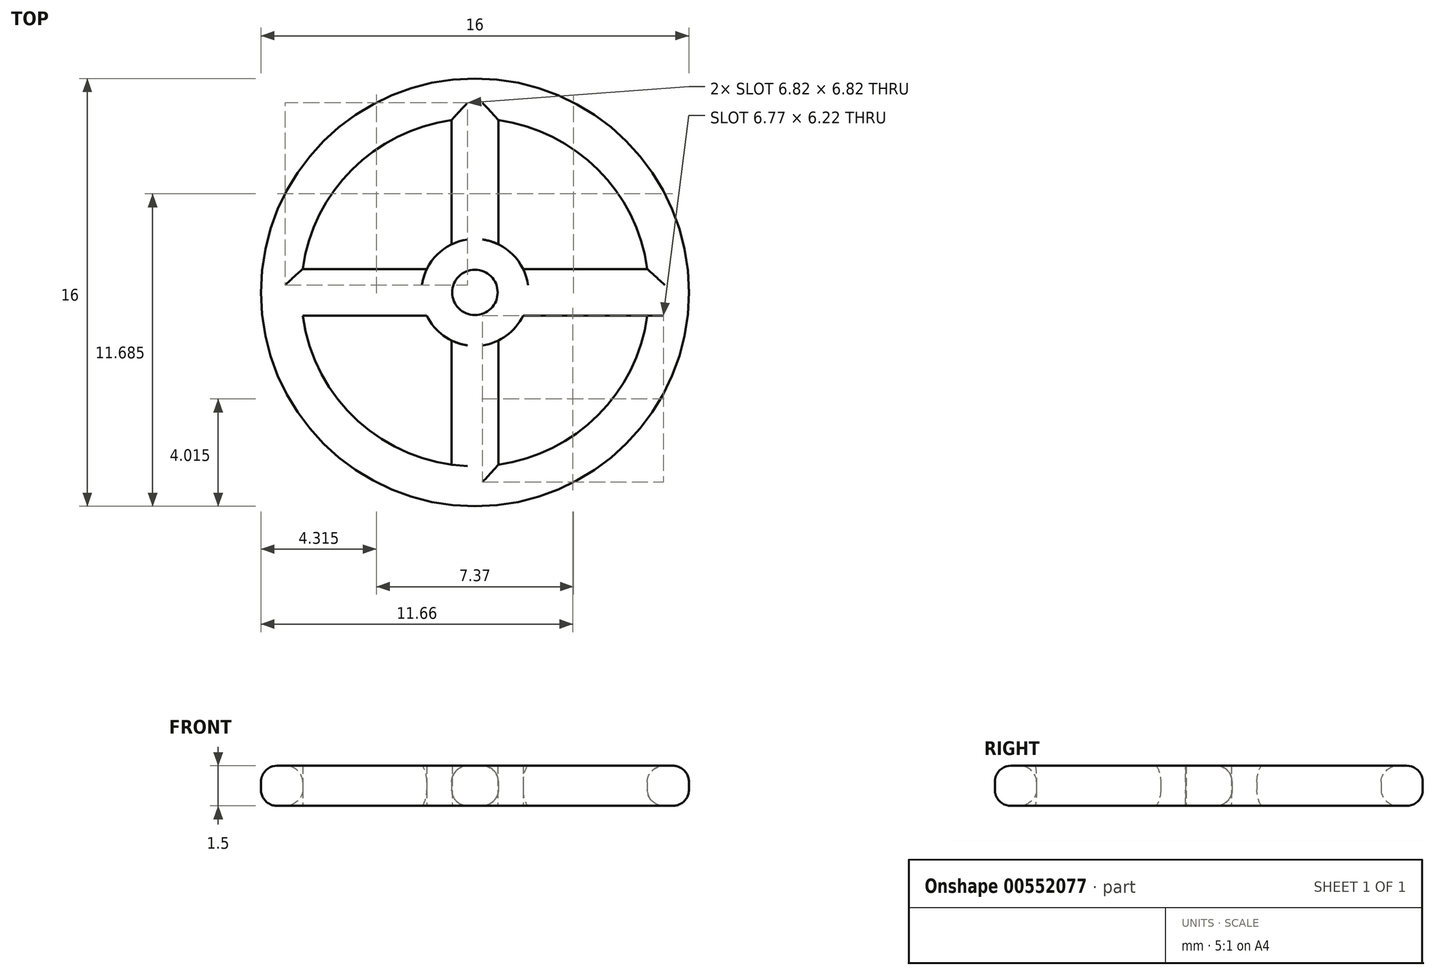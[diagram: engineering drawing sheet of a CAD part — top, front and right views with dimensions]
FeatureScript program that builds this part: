
annotation { "Feature Type Name" : "Feature", "Feature Type Description" : "" }
export const myFeature = defineFeature(function(context is Context, id is Id, definition is map)
    precondition{}
    {
        {
            var Q0;
            Q0=qCreatedBy(makeId("Top.planeOp"),FACE);
            var sketch = newSketch(context, id + "F0", { "sketchPlane" : qUnion([Q0])});
            skCircle(sketch, "E0", {"center": v(0, 0) * mm, "radius": 8 * mm});
            skCircle(sketch, "E1", {"center": v(0, 0) * mm, "radius": 6.5 * mm});
            skLineSegment(sketch, "E2.bottom", {"start": v(7.37, -0.87) * mm, "end": v(-7.37, -0.88) * mm});
            skLineSegment(sketch, "E2.top", {"start": v(7.37, 0.88) * mm, "end": v(-7.37, 0.87) * mm});
            skLineSegment(sketch, "E2.left", {"start": v(7.37, -0.87) * mm, "end": v(7.37, 0.88) * mm});
            skLineSegment(sketch, "E2.right", {"start": v(-7.37, -0.88) * mm, "end": v(-7.37, 0.87) * mm});
            skLineSegment(sketch, "E3.bottom", {"start": v(0.88, 6.98) * mm, "end": v(-0.88, 6.98) * mm});
            skLineSegment(sketch, "E3.top", {"start": v(0.88, -6.98) * mm, "end": v(-0.88, -6.98) * mm});
            skLineSegment(sketch, "E3.left", {"start": v(0.88, 6.98) * mm, "end": v(0.88, -6.98) * mm});
            skLineSegment(sketch, "E3.right", {"start": v(-0.88, 6.98) * mm, "end": v(-0.88, -6.98) * mm});
            skCircle(sketch, "E4", {"center": v(0, 0) * mm, "radius": 0.85 * mm});
            skCircle(sketch, "E5", {"center": v(0, 0) * mm, "radius": 2 * mm});
            skSolve(sketch);
        }
        {
            var Q0;
            {var subQ5=sQuery(id+"F0.wireOp",EDGE,"E2.right");Q0=makeQuery(id+"F0.imprint","IMPRINT",FACE,{"disambiguationData":[TD([[makeQuery(id+"F0.imprint","IMPRINT",EDGE,{"derivedFrom":subQ5}),-1.0]])]});}
            var Q1;
            {var subQ0=sQuery(id+"F0.wireOp",EDGE,"E2.top");var subQ1=sQuery(id+"F0.wireOp",EDGE,"E1");var subQ2=makeQuery(id+"F0.imprint","INTERSECT",VERTEX,{"disambiguationData":[OD(1.0)],"derivedFrom":[subQ1,subQ0]});Q1=makeQuery(id+"F0.imprint","IMPRINT",FACE,{"disambiguationData":[TD([[makeQuery(id+"F0.imprint","IMPRINT",EDGE,{"disambiguationData":[TD([[subQ2,-1.0]])],"derivedFrom":subQ1}),1.0]])]});}
            var Q2;
            Q2=makeQuery(id+"F0.imprint","IMPRINT",FACE,{"disambiguationData":[TD([[makeQuery(id+"F0.imprint","IMPRINT",EDGE,{"derivedFrom":sQuery(id+"F0.wireOp",EDGE,"E0")}),1.0]])]});
            var Q3;
            {var subQ5=sQuery(id+"F0.wireOp",EDGE,"E3.bottom");Q3=makeQuery(id+"F0.imprint","IMPRINT",FACE,{"disambiguationData":[TD([[makeQuery(id+"F0.imprint","IMPRINT",EDGE,{"derivedFrom":subQ5}),1.0]])]});}
            var Q4;
            {var subQ0=sQuery(id+"F0.wireOp",EDGE,"E3.left");var subQ1=sQuery(id+"F0.wireOp",EDGE,"E1");var subQ2=makeQuery(id+"F0.imprint","INTERSECT",VERTEX,{"disambiguationData":[OD(0.0)],"derivedFrom":[subQ1,subQ0]});Q4=makeQuery(id+"F0.imprint","IMPRINT",FACE,{"disambiguationData":[TD([[makeQuery(id+"F0.imprint","IMPRINT",EDGE,{"disambiguationData":[TD([[subQ2,-1.0]])],"derivedFrom":subQ1}),1.0]])]});}
            var Q5;
            {var subQ0=sQuery(id+"F0.wireOp",EDGE,"E5");var subQ1=sQuery(id+"F0.wireOp",EDGE,"E2.top");var subQ2=makeQuery(id+"F0.imprint","INTERSECT",VERTEX,{"disambiguationData":[OD(0.0)],"derivedFrom":[subQ1,subQ0]});Q5=makeQuery(id+"F0.imprint","IMPRINT",FACE,{"disambiguationData":[TD([[makeQuery(id+"F0.imprint","IMPRINT",EDGE,{"disambiguationData":[TD([[subQ2,-1.0]])],"derivedFrom":subQ1}),-1.0]])]});}
            var Q6;
            {var subQ0=sQuery(id+"F0.wireOp",EDGE,"E3.left");var subQ1=sQuery(id+"F0.wireOp",EDGE,"E2.top");var subQ2=makeQuery(id+"F0.imprint","INTERSECT",VERTEX,{"derivedFrom":[subQ1,subQ0]});Q6=makeQuery(id+"F0.imprint","IMPRINT",FACE,{"disambiguationData":[TD([[makeQuery(id+"F0.imprint","IMPRINT",EDGE,{"disambiguationData":[TD([[subQ2,-1.0]])],"derivedFrom":subQ1}),-1.0]])]});}
            var Q7;
            {var subQ0=sQuery(id+"F0.wireOp",EDGE,"E3.right");var subQ1=sQuery(id+"F0.wireOp",EDGE,"E2.top");var subQ2=makeQuery(id+"F0.imprint","INTERSECT",VERTEX,{"derivedFrom":[subQ1,subQ0]});Q7=makeQuery(id+"F0.imprint","IMPRINT",FACE,{"disambiguationData":[TD([[makeQuery(id+"F0.imprint","IMPRINT",EDGE,{"disambiguationData":[TD([[subQ2,-1.0]])],"derivedFrom":subQ1}),-1.0]])]});}
            var Q8;
            {var subQ0=sQuery(id+"F0.wireOp",EDGE,"E3.right");var subQ1=sQuery(id+"F0.wireOp",EDGE,"E2.bottom");var subQ2=makeQuery(id+"F0.imprint","INTERSECT",VERTEX,{"derivedFrom":[subQ1,subQ0]});Q8=makeQuery(id+"F0.imprint","IMPRINT",FACE,{"disambiguationData":[TD([[makeQuery(id+"F0.imprint","IMPRINT",EDGE,{"disambiguationData":[TD([[subQ2,-1.0]])],"derivedFrom":subQ1}),-1.0]])]});}
            var Q9;
            {var subQ0=sQuery(id+"F0.wireOp",EDGE,"E3.right");var subQ1=sQuery(id+"F0.wireOp",EDGE,"E2.bottom");var subQ2=makeQuery(id+"F0.imprint","INTERSECT",VERTEX,{"derivedFrom":[subQ1,subQ0]});Q9=makeQuery(id+"F0.imprint","IMPRINT",FACE,{"disambiguationData":[TD([[makeQuery(id+"F0.imprint","IMPRINT",EDGE,{"disambiguationData":[TD([[subQ2,-1.0]])],"derivedFrom":subQ1}),1.0]])]});}
            var Q10;
            {var subQ0=sQuery(id+"F0.wireOp",EDGE,"E3.left");var subQ1=sQuery(id+"F0.wireOp",EDGE,"E2.bottom");var subQ2=makeQuery(id+"F0.imprint","INTERSECT",VERTEX,{"derivedFrom":[subQ1,subQ0]});Q10=makeQuery(id+"F0.imprint","IMPRINT",FACE,{"disambiguationData":[TD([[makeQuery(id+"F0.imprint","IMPRINT",EDGE,{"disambiguationData":[TD([[subQ2,-1.0]])],"derivedFrom":subQ1}),1.0]])]});}
            var Q11;
            Q11=makeQuery(id+"F0.imprint","IMPRINT",FACE,{"disambiguationData":[TD([[makeQuery(id+"F0.imprint","IMPRINT",EDGE,{"derivedFrom":sQuery(id+"F0.wireOp",EDGE,"E4")}),-1.0]])]});
            var Q12;
            {var subQ0=sQuery(id+"F0.wireOp",EDGE,"E5");var subQ1=sQuery(id+"F0.wireOp",EDGE,"E2.bottom");var subQ2=makeQuery(id+"F0.imprint","INTERSECT",VERTEX,{"disambiguationData":[OD(0.0)],"derivedFrom":[subQ1,subQ0]});Q12=makeQuery(id+"F0.imprint","IMPRINT",FACE,{"disambiguationData":[TD([[makeQuery(id+"F0.imprint","IMPRINT",EDGE,{"disambiguationData":[TD([[subQ2,-1.0]])],"derivedFrom":subQ1}),-1.0]])]});}
            var Q13;
            {var subQ0=sQuery(id+"F0.wireOp",EDGE,"E5");var subQ1=sQuery(id+"F0.wireOp",EDGE,"E2.bottom");var subQ2=makeQuery(id+"F0.imprint","INTERSECT",VERTEX,{"disambiguationData":[OD(0.0)],"derivedFrom":[subQ1,subQ0]});Q13=makeQuery(id+"F0.imprint","IMPRINT",FACE,{"disambiguationData":[TD([[makeQuery(id+"F0.imprint","IMPRINT",EDGE,{"disambiguationData":[TD([[subQ2,-1.0]])],"derivedFrom":subQ1}),1.0]])]});}
            var Q14;
            {var subQ0=sQuery(id+"F0.wireOp",EDGE,"E2.top");var subQ1=sQuery(id+"F0.wireOp",EDGE,"E1");var subQ2=makeQuery(id+"F0.imprint","INTERSECT",VERTEX,{"disambiguationData":[OD(0.0)],"derivedFrom":[subQ1,subQ0]});Q14=makeQuery(id+"F0.imprint","IMPRINT",FACE,{"disambiguationData":[TD([[makeQuery(id+"F0.imprint","IMPRINT",EDGE,{"disambiguationData":[TD([[subQ2,1.0]])],"derivedFrom":subQ1}),1.0]])]});}
            var Q15;
            {var subQ0=sQuery(id+"F0.wireOp",EDGE,"E3.right");var subQ1=sQuery(id+"F0.wireOp",EDGE,"E1");var subQ2=makeQuery(id+"F0.imprint","INTERSECT",VERTEX,{"disambiguationData":[OD(1.0)],"derivedFrom":[subQ1,subQ0]});Q15=makeQuery(id+"F0.imprint","IMPRINT",FACE,{"disambiguationData":[TD([[makeQuery(id+"F0.imprint","IMPRINT",EDGE,{"disambiguationData":[TD([[subQ2,-1.0]])],"derivedFrom":subQ1}),1.0]])]});}
            var Q16;
            {var subQ5=sQuery(id+"F0.wireOp",EDGE,"E2.left");Q16=makeQuery(id+"F0.imprint","IMPRINT",FACE,{"disambiguationData":[TD([[makeQuery(id+"F0.imprint","IMPRINT",EDGE,{"derivedFrom":subQ5}),1.0]])]});}
            var Q17;
            {var subQ5=sQuery(id+"F0.wireOp",EDGE,"E3.top");Q17=makeQuery(id+"F0.imprint","IMPRINT",FACE,{"disambiguationData":[TD([[makeQuery(id+"F0.imprint","IMPRINT",EDGE,{"derivedFrom":subQ5}),-1.0]])]});}
            extrude(context, id + "F1", {"entities" : qUnion([Q0, Q1, Q2, Q3, Q4, Q5, Q6, Q7, Q8, Q9, Q10, Q11, Q12, Q13, Q14, Q15, Q16, Q17]), "depth" : .75 * mm, "offsetDistance" : 25 * mm, "hasSecondDirection" : true, "secondDirectionOppositeDirection" : true, "secondDirectionDepth" : .75 * mm});
        }
        {
            var Q0;
            Q0=makeQuery(id+"F1.opExtrude","CAP_EDGE",EDGE,{"disambiguationData":[OSD([sQuery(id+"F0.wireOp",EDGE,"E0")])],"isStart":false});
            var Q1;
            {var subQ0=sQuery(id+"F0.wireOp",EDGE,"E1");Q1=makeQuery(id+"F1.opExtrude","CAP_EDGE",EDGE,{"disambiguationData":[OSD([subQ0]),TDD([makeQuery(id+"F0.imprint","IMPRINT",EDGE,{"disambiguationData":[TD([[makeQuery(id+"F0.imprint","INTERSECT",VERTEX,{"disambiguationData":[OD(0.0)],"derivedFrom":[subQ0,sQuery(id+"F0.wireOp",EDGE,"E2.bottom")]}),-1.0]])],"derivedFrom":subQ0})])],"isStart":false});}
            var Q2;
            {var subQ0=sQuery(id+"F0.wireOp",EDGE,"E2.bottom");Q2=makeQuery(id+"F1.opExtrude","CAP_EDGE",EDGE,{"disambiguationData":[OSD([subQ0]),TDD([makeQuery(id+"F0.imprint","IMPRINT",EDGE,{"disambiguationData":[TD([[makeQuery(id+"F0.imprint","INTERSECT",VERTEX,{"disambiguationData":[OD(0.0)],"derivedFrom":[sQuery(id+"F0.wireOp",EDGE,"E1"),subQ0]}),1.0]])],"derivedFrom":subQ0})])],"isStart":false});}
            var Q3;
            {var subQ0=sQuery(id+"F0.wireOp",EDGE,"E2.top");Q3=makeQuery(id+"F1.opExtrude","CAP_EDGE",EDGE,{"disambiguationData":[OSD([subQ0]),TDD([makeQuery(id+"F0.imprint","IMPRINT",EDGE,{"disambiguationData":[TD([[makeQuery(id+"F0.imprint","INTERSECT",VERTEX,{"disambiguationData":[OD(1.0)],"derivedFrom":[sQuery(id+"F0.wireOp",EDGE,"E1"),subQ0]}),1.0]])],"derivedFrom":subQ0})])],"isStart":false});}
            var Q4;
            {var subQ0=sQuery(id+"F0.wireOp",EDGE,"E3.right");Q4=makeQuery(id+"F1.opExtrude","CAP_EDGE",EDGE,{"disambiguationData":[OSD([subQ0]),TDD([makeQuery(id+"F0.imprint","IMPRINT",EDGE,{"disambiguationData":[TD([[makeQuery(id+"F0.imprint","INTERSECT",VERTEX,{"disambiguationData":[OD(0.0)],"derivedFrom":[sQuery(id+"F0.wireOp",EDGE,"E1"),subQ0]}),-1.0]])],"derivedFrom":subQ0})])],"isStart":false});}
            var Q5;
            {var subQ0=sQuery(id+"F0.wireOp",EDGE,"E3.left");Q5=makeQuery(id+"F1.opExtrude","CAP_EDGE",EDGE,{"disambiguationData":[OSD([subQ0]),TDD([makeQuery(id+"F0.imprint","IMPRINT",EDGE,{"disambiguationData":[TD([[makeQuery(id+"F0.imprint","INTERSECT",VERTEX,{"disambiguationData":[OD(0.0)],"derivedFrom":[sQuery(id+"F0.wireOp",EDGE,"E1"),subQ0]}),-1.0]])],"derivedFrom":subQ0})])],"isStart":false});}
            var Q6;
            {var subQ0=sQuery(id+"F0.wireOp",EDGE,"E1");Q6=makeQuery(id+"F1.opExtrude","CAP_EDGE",EDGE,{"disambiguationData":[OSD([subQ0]),TDD([makeQuery(id+"F0.imprint","IMPRINT",EDGE,{"disambiguationData":[TD([[makeQuery(id+"F0.imprint","INTERSECT",VERTEX,{"disambiguationData":[OD(0.0)],"derivedFrom":[subQ0,sQuery(id+"F0.wireOp",EDGE,"E3.right")]}),-1.0]])],"derivedFrom":subQ0})])],"isStart":false});}
            var Q7;
            {var subQ0=sQuery(id+"F0.wireOp",EDGE,"E1");Q7=makeQuery(id+"F1.opExtrude","CAP_EDGE",EDGE,{"disambiguationData":[OSD([subQ0]),TDD([makeQuery(id+"F0.imprint","IMPRINT",EDGE,{"disambiguationData":[TD([[makeQuery(id+"F0.imprint","INTERSECT",VERTEX,{"disambiguationData":[OD(0.0)],"derivedFrom":[subQ0,sQuery(id+"F0.wireOp",EDGE,"E3.left")]}),1.0]])],"derivedFrom":subQ0})])],"isStart":false});}
            var Q8;
            {var subQ0=sQuery(id+"F0.wireOp",EDGE,"E2.top");Q8=makeQuery(id+"F1.opExtrude","CAP_EDGE",EDGE,{"disambiguationData":[OSD([subQ0]),TDD([makeQuery(id+"F0.imprint","IMPRINT",EDGE,{"disambiguationData":[TD([[makeQuery(id+"F0.imprint","INTERSECT",VERTEX,{"disambiguationData":[OD(0.0)],"derivedFrom":[sQuery(id+"F0.wireOp",EDGE,"E1"),subQ0]}),-1.0]])],"derivedFrom":subQ0})])],"isStart":false});}
            var Q9;
            {var subQ0=sQuery(id+"F0.wireOp",EDGE,"E2.bottom");Q9=makeQuery(id+"F1.opExtrude","CAP_EDGE",EDGE,{"disambiguationData":[OSD([subQ0]),TDD([makeQuery(id+"F0.imprint","IMPRINT",EDGE,{"disambiguationData":[TD([[makeQuery(id+"F0.imprint","INTERSECT",VERTEX,{"disambiguationData":[OD(1.0)],"derivedFrom":[sQuery(id+"F0.wireOp",EDGE,"E1"),subQ0]}),-1.0]])],"derivedFrom":subQ0})])],"isStart":false});}
            var Q10;
            {var subQ0=sQuery(id+"F0.wireOp",EDGE,"E1");Q10=makeQuery(id+"F1.opExtrude","CAP_EDGE",EDGE,{"disambiguationData":[OSD([subQ0]),TDD([makeQuery(id+"F0.imprint","IMPRINT",EDGE,{"disambiguationData":[TD([[makeQuery(id+"F0.imprint","INTERSECT",VERTEX,{"disambiguationData":[OD(1.0)],"derivedFrom":[subQ0,sQuery(id+"F0.wireOp",EDGE,"E3.left")]}),-1.0]])],"derivedFrom":subQ0})])],"isStart":false});}
            var Q11;
            {var subQ0=sQuery(id+"F0.wireOp",EDGE,"E3.left");Q11=makeQuery(id+"F1.opExtrude","CAP_EDGE",EDGE,{"disambiguationData":[OSD([subQ0]),TDD([makeQuery(id+"F0.imprint","IMPRINT",EDGE,{"disambiguationData":[TD([[makeQuery(id+"F0.imprint","INTERSECT",VERTEX,{"disambiguationData":[OD(1.0)],"derivedFrom":[sQuery(id+"F0.wireOp",EDGE,"E1"),subQ0]}),1.0]])],"derivedFrom":subQ0})])],"isStart":false});}
            var Q12;
            {var subQ0=sQuery(id+"F0.wireOp",EDGE,"E3.right");Q12=makeQuery(id+"F1.opExtrude","CAP_EDGE",EDGE,{"disambiguationData":[OSD([subQ0]),TDD([makeQuery(id+"F0.imprint","IMPRINT",EDGE,{"disambiguationData":[TD([[makeQuery(id+"F0.imprint","INTERSECT",VERTEX,{"disambiguationData":[OD(1.0)],"derivedFrom":[sQuery(id+"F0.wireOp",EDGE,"E1"),subQ0]}),1.0]])],"derivedFrom":subQ0})])],"isStart":false});}
            var Q13;
            Q13=makeQuery(id+"F1.opExtrude","CAP_EDGE",EDGE,{"disambiguationData":[OSD([sQuery(id+"F0.wireOp",EDGE,"E0")])],"isStart":true});
            var Q14;
            {var subQ0=sQuery(id+"F0.wireOp",EDGE,"E1");Q14=makeQuery(id+"F1.opExtrude","CAP_EDGE",EDGE,{"disambiguationData":[OSD([subQ0]),TDD([makeQuery(id+"F0.imprint","IMPRINT",EDGE,{"disambiguationData":[TD([[makeQuery(id+"F0.imprint","INTERSECT",VERTEX,{"disambiguationData":[OD(1.0)],"derivedFrom":[subQ0,sQuery(id+"F0.wireOp",EDGE,"E3.left")]}),-1.0]])],"derivedFrom":subQ0})])],"isStart":true});}
            var Q15;
            {var subQ0=sQuery(id+"F0.wireOp",EDGE,"E2.bottom");Q15=makeQuery(id+"F1.opExtrude","CAP_EDGE",EDGE,{"disambiguationData":[OSD([subQ0]),TDD([makeQuery(id+"F0.imprint","IMPRINT",EDGE,{"disambiguationData":[TD([[makeQuery(id+"F0.imprint","INTERSECT",VERTEX,{"disambiguationData":[OD(1.0)],"derivedFrom":[sQuery(id+"F0.wireOp",EDGE,"E1"),subQ0]}),-1.0]])],"derivedFrom":subQ0})])],"isStart":true});}
            var Q16;
            {var subQ0=sQuery(id+"F0.wireOp",EDGE,"E3.left");Q16=makeQuery(id+"F1.opExtrude","CAP_EDGE",EDGE,{"disambiguationData":[OSD([subQ0]),TDD([makeQuery(id+"F0.imprint","IMPRINT",EDGE,{"disambiguationData":[TD([[makeQuery(id+"F0.imprint","INTERSECT",VERTEX,{"disambiguationData":[OD(1.0)],"derivedFrom":[sQuery(id+"F0.wireOp",EDGE,"E1"),subQ0]}),1.0]])],"derivedFrom":subQ0})])],"isStart":true});}
            var Q17;
            {var subQ0=sQuery(id+"F0.wireOp",EDGE,"E3.right");Q17=makeQuery(id+"F1.opExtrude","CAP_EDGE",EDGE,{"disambiguationData":[OSD([subQ0]),TDD([makeQuery(id+"F0.imprint","IMPRINT",EDGE,{"disambiguationData":[TD([[makeQuery(id+"F0.imprint","INTERSECT",VERTEX,{"disambiguationData":[OD(1.0)],"derivedFrom":[sQuery(id+"F0.wireOp",EDGE,"E1"),subQ0]}),1.0]])],"derivedFrom":subQ0})])],"isStart":true});}
            var Q18;
            {var subQ0=sQuery(id+"F0.wireOp",EDGE,"E1");Q18=makeQuery(id+"F1.opExtrude","CAP_EDGE",EDGE,{"disambiguationData":[OSD([subQ0]),TDD([makeQuery(id+"F0.imprint","IMPRINT",EDGE,{"disambiguationData":[TD([[makeQuery(id+"F0.imprint","INTERSECT",VERTEX,{"disambiguationData":[OD(0.0)],"derivedFrom":[subQ0,sQuery(id+"F0.wireOp",EDGE,"E2.bottom")]}),-1.0]])],"derivedFrom":subQ0})])],"isStart":true});}
            var Q19;
            {var subQ0=sQuery(id+"F0.wireOp",EDGE,"E2.bottom");Q19=makeQuery(id+"F1.opExtrude","CAP_EDGE",EDGE,{"disambiguationData":[OSD([subQ0]),TDD([makeQuery(id+"F0.imprint","IMPRINT",EDGE,{"disambiguationData":[TD([[makeQuery(id+"F0.imprint","INTERSECT",VERTEX,{"disambiguationData":[OD(0.0)],"derivedFrom":[sQuery(id+"F0.wireOp",EDGE,"E1"),subQ0]}),1.0]])],"derivedFrom":subQ0})])],"isStart":true});}
            var Q20;
            {var subQ0=sQuery(id+"F0.wireOp",EDGE,"E2.top");Q20=makeQuery(id+"F1.opExtrude","CAP_EDGE",EDGE,{"disambiguationData":[OSD([subQ0]),TDD([makeQuery(id+"F0.imprint","IMPRINT",EDGE,{"disambiguationData":[TD([[makeQuery(id+"F0.imprint","INTERSECT",VERTEX,{"disambiguationData":[OD(1.0)],"derivedFrom":[sQuery(id+"F0.wireOp",EDGE,"E1"),subQ0]}),1.0]])],"derivedFrom":subQ0})])],"isStart":true});}
            var Q21;
            {var subQ0=sQuery(id+"F0.wireOp",EDGE,"E1");Q21=makeQuery(id+"F1.opExtrude","CAP_EDGE",EDGE,{"disambiguationData":[OSD([subQ0]),TDD([makeQuery(id+"F0.imprint","IMPRINT",EDGE,{"disambiguationData":[TD([[makeQuery(id+"F0.imprint","INTERSECT",VERTEX,{"disambiguationData":[OD(0.0)],"derivedFrom":[subQ0,sQuery(id+"F0.wireOp",EDGE,"E3.right")]}),-1.0]])],"derivedFrom":subQ0})])],"isStart":true});}
            var Q22;
            {var subQ0=sQuery(id+"F0.wireOp",EDGE,"E1");Q22=makeQuery(id+"F1.opExtrude","CAP_EDGE",EDGE,{"disambiguationData":[OSD([subQ0]),TDD([makeQuery(id+"F0.imprint","IMPRINT",EDGE,{"disambiguationData":[TD([[makeQuery(id+"F0.imprint","INTERSECT",VERTEX,{"disambiguationData":[OD(0.0)],"derivedFrom":[subQ0,sQuery(id+"F0.wireOp",EDGE,"E3.left")]}),1.0]])],"derivedFrom":subQ0})])],"isStart":true});}
            var Q23;
            {var subQ0=sQuery(id+"F0.wireOp",EDGE,"E2.top");Q23=makeQuery(id+"F1.opExtrude","CAP_EDGE",EDGE,{"disambiguationData":[OSD([subQ0]),TDD([makeQuery(id+"F0.imprint","IMPRINT",EDGE,{"disambiguationData":[TD([[makeQuery(id+"F0.imprint","INTERSECT",VERTEX,{"disambiguationData":[OD(0.0)],"derivedFrom":[sQuery(id+"F0.wireOp",EDGE,"E1"),subQ0]}),-1.0]])],"derivedFrom":subQ0})])],"isStart":true});}
            var Q24;
            {var subQ0=sQuery(id+"F0.wireOp",EDGE,"E3.right");Q24=makeQuery(id+"F1.opExtrude","CAP_EDGE",EDGE,{"disambiguationData":[OSD([subQ0]),TDD([makeQuery(id+"F0.imprint","IMPRINT",EDGE,{"disambiguationData":[TD([[makeQuery(id+"F0.imprint","INTERSECT",VERTEX,{"disambiguationData":[OD(0.0)],"derivedFrom":[sQuery(id+"F0.wireOp",EDGE,"E1"),subQ0]}),-1.0]])],"derivedFrom":subQ0})])],"isStart":true});}
            var Q25;
            {var subQ0=sQuery(id+"F0.wireOp",EDGE,"E3.left");Q25=makeQuery(id+"F1.opExtrude","CAP_EDGE",EDGE,{"disambiguationData":[OSD([subQ0]),TDD([makeQuery(id+"F0.imprint","IMPRINT",EDGE,{"disambiguationData":[TD([[makeQuery(id+"F0.imprint","INTERSECT",VERTEX,{"disambiguationData":[OD(0.0)],"derivedFrom":[sQuery(id+"F0.wireOp",EDGE,"E1"),subQ0]}),-1.0]])],"derivedFrom":subQ0})])],"isStart":true});}
            fillet(context, id + "F2", {"entities" : qUnion([Q0, Q1, Q2, Q3, Q4, Q5, Q6, Q7, Q8, Q9, Q10, Q11, Q12, Q13, Q14, Q15, Q16, Q17, Q18, Q19, Q20, Q21, Q22, Q23, Q24, Q25]), "radius" : .6 * mm, "tangentPropagation" : true, "allowEdgeOverflow" : false});
        }
    });
